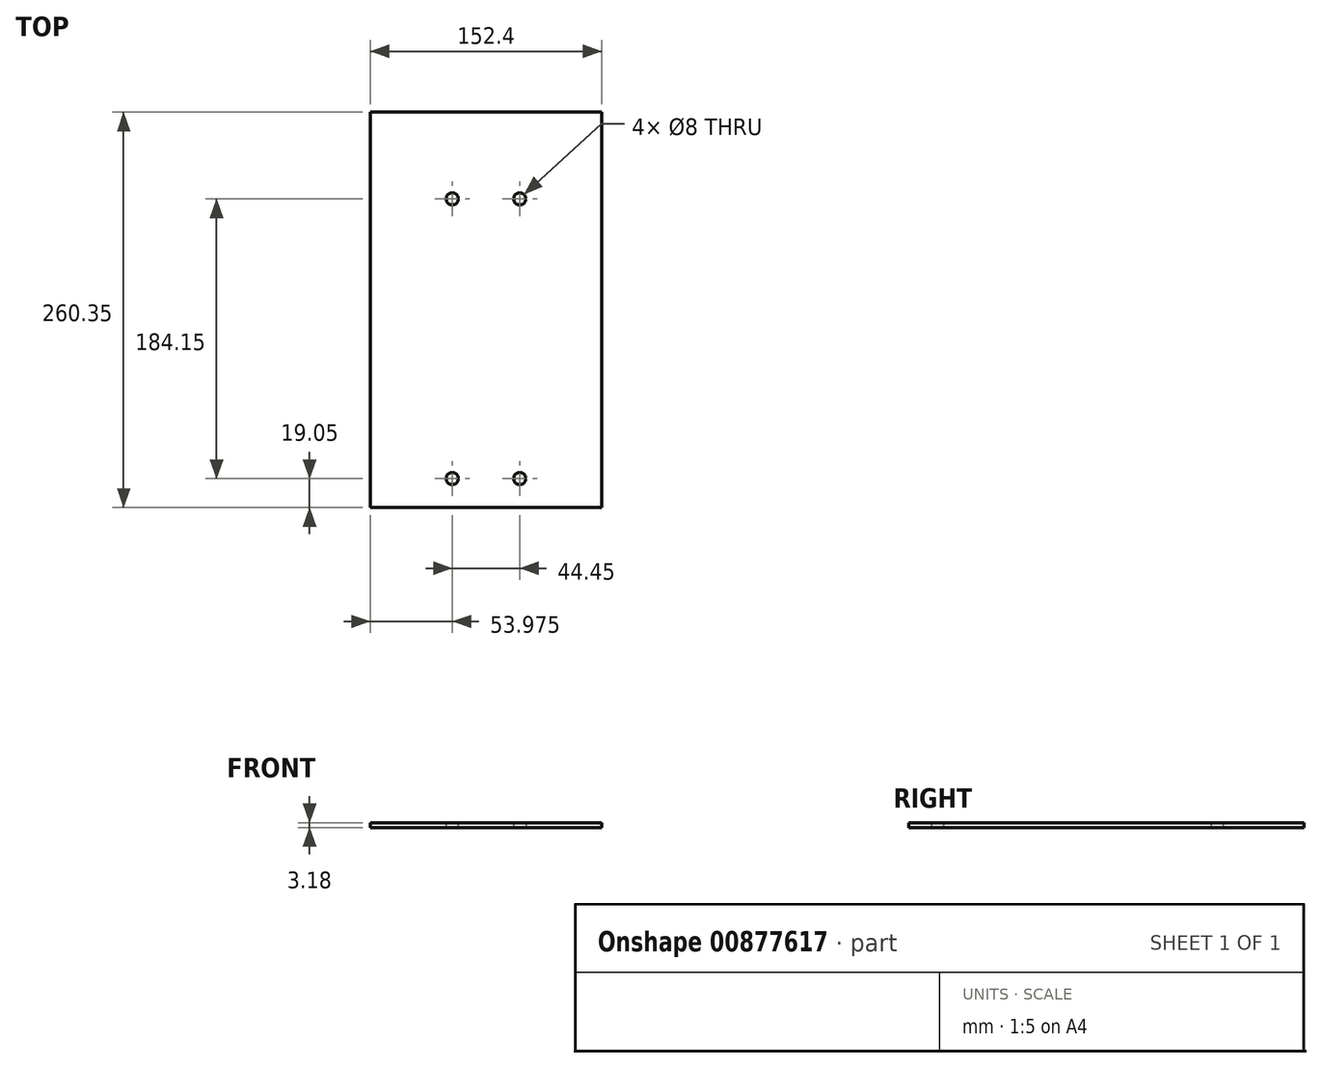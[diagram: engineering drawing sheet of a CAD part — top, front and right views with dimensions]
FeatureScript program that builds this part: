
annotation { "Feature Type Name" : "Feature", "Feature Type Description" : "" }
export const myFeature = defineFeature(function(context is Context, id is Id, definition is map)
    precondition{}
    {
        {
            var Q0;
            Q0=qCreatedBy(makeId("Top.planeOp"),FACE);
            var sketch = newSketch(context, id + "F0", { "sketchPlane" : qUnion([Q0])});
            skLineSegment(sketch, "E0.bottom", {"start": v(0, 0) * mm, "end": v(152.4, 0) * mm});
            skLineSegment(sketch, "E0.top", {"start": v(0, 260.35) * mm, "end": v(152.4, 260.35) * mm});
            skLineSegment(sketch, "E0.left", {"start": v(0, 0) * mm, "end": v(0, 260.35) * mm});
            skLineSegment(sketch, "E0.right", {"start": v(152.4, 0) * mm, "end": v(152.4, 260.35) * mm});
            skCircle(sketch, "E1", {"center": v(53.98, 19.05) * mm, "radius": 4 * mm});
            skCircle(sketch, "E2", {"center": v(98.43, 19.05) * mm, "radius": 4 * mm});
            skCircle(sketch, "E3", {"center": v(98.42, 203.2) * mm, "radius": 4 * mm});
            skCircle(sketch, "E4", {"center": v(53.97, 203.2) * mm, "radius": 4 * mm});
            skSolve(sketch);
        }
        {
            var Q0;
            Q0 = qSketchRegion(id + "F0", true);
            extrude(context, id + "F1", {"entities" : qUnion([Q0]), "depth" : 3.17 * mm, "offsetDistance" : 25.4 * mm});
        }
    });
